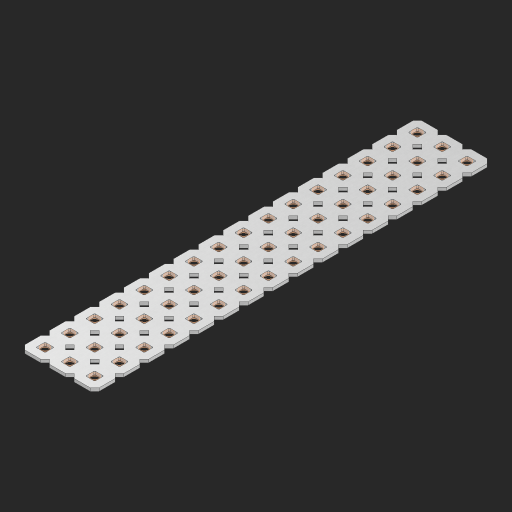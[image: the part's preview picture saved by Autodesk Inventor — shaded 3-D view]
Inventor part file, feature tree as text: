
AUTODESK INVENTOR PART (.ipt)
format: ipt  version: 2023 (Build 270158000, 158)  size: 834,560 bytes
history: native  units: in
note: dims shown in document units (in); Inventor stores cm internally (conversion verified against a paired STEP export)
features: other x49, extrude x47, sketch x2, pattern_linear x1
ambient origin geometry x8: Origin, YZ Plane, XZ Plane, XY Plane, X Axis, Y Axis, Z Axis, Center Point
bodies: Solid1 (feature_tree), Body (feature_tree)
feature tree (99):
  pattern_linear  "Rectangular Pattern1"  Spacing1=0.09in  [1 undecoded]
  sketch  "Sketch1"  dims[d1=0.5in]
  sketch  "Sketch2"  dims[d2=0.182in d3=0.09in d4=0.09in d5=0.09in d6=0.09in d7=0.09in d8=0.09in d9=0.09in d10=0.09in d11=0.02in d13=0.0in d14=0.172in d15=0.0625in d16=0.0in d19=0.5in d22=0.5in]
  other  "Srf1"
  other  "Srf126"
  other  "Srf127"
  other  "Srf128"
  other  "Srf129"
  other  "Srf130"
  other  "Srf131"
  other  "Srf250"
  other  "Srf251"
  other  "Srf252"
  other  "Srf253"
  other  "Srf254"
  other  "Srf255"
  other  "Srf256"
  other  "Srf257"
  other  "Srf258"
  other  "Srf268"
  other  "Srf269"
  other  "Srf270"
  other  "Srf271"
  other  "Srf272"
  other  "Srf273"
  other  "Srf274"
  other  "Srf275"
  other  "Srf276"
  other  "Srf277"
  other  "Srf278"
  other  "Srf279"
  other  "Srf280"
  other  "Srf281"
  other  "Srf282"
  other  "Srf283"
  other  "Srf293"
  other  "Srf294"
  other  "Srf295"
  other  "Srf296"
  other  "Srf297"
  other  "Srf298"
  other  "Srf299"
  other  "Srf300"
  other  "Srf301"
  other  "Srf302"
  other  "Srf303"
  other  "Srf304"
  other  "Srf305"
  other  "Srf306"
  other  "Srf307"
  other  "Srf308"
  other  "Circle"
  extrude  "ExtrusionSrf126"  Depth=0.09in
  extrude  "ExtrusionSrf127"  Depth=0.09in
  extrude  "ExtrusionSrf128"  Depth=0.09in
  extrude  "ExtrusionSrf129"  Depth=0.09in
  extrude  "ExtrusionSrf130"  Depth=0.09in
  extrude  "ExtrusionSrf131"  Depth=0.09in
  extrude  "ExtrusionSrf250"  Depth=0.09in
  extrude  "ExtrusionSrf251"  Depth=0.02in
  extrude  "ExtrusionSrf252"  TaperAngle=0.0deg  [1 undecoded]
  extrude  "ExtrusionSrf253"  Depth=0.5in
  extrude  "ExtrusionSrf254"  Depth=0.0625in TaperAngle=0.0deg
  extrude  "ExtrusionSrf255"  Depth=0.5in
  extrude  "ExtrusionSrf256"  Depth=0.5in
  extrude  "ExtrusionSrf257"  [1 undecoded]
  extrude  "ExtrusionSrf258"  [1 undecoded]
  extrude  "ExtrusionSrf268"  [1 undecoded]
  extrude  "ExtrusionSrf269"  [1 undecoded]
  extrude  "ExtrusionSrf270"  [1 undecoded]
  extrude  "ExtrusionSrf271"  [1 undecoded]
  extrude  "ExtrusionSrf272"  [1 undecoded]
  extrude  "ExtrusionSrf273"  [1 undecoded]
  extrude  "ExtrusionSrf274"  [1 undecoded]
  extrude  "ExtrusionSrf275"  [1 undecoded]
  extrude  "ExtrusionSrf276"  [1 undecoded]
  extrude  "ExtrusionSrf277"  [1 undecoded]
  extrude  "ExtrusionSrf278"  [1 undecoded]
  extrude  "ExtrusionSrf279"  [1 undecoded]
  extrude  "ExtrusionSrf280"  [1 undecoded]
  extrude  "ExtrusionSrf281"  [1 undecoded]
  extrude  "ExtrusionSrf282"  [1 undecoded]
  extrude  "ExtrusionSrf283"  [1 undecoded]
  extrude  "ExtrusionSrf293"  [1 undecoded]
  extrude  "ExtrusionSrf294"  [1 undecoded]
  extrude  "ExtrusionSrf295"  [1 undecoded]
  extrude  "ExtrusionSrf296"  [1 undecoded]
  extrude  "ExtrusionSrf297"  [1 undecoded]
  extrude  "ExtrusionSrf298"  [1 undecoded]
  extrude  "ExtrusionSrf299"  [1 undecoded]
  extrude  "ExtrusionSrf300"  [1 undecoded]
  extrude  "ExtrusionSrf301"  [1 undecoded]
  extrude  "ExtrusionSrf302"  [1 undecoded]
  extrude  "ExtrusionSrf303"  [1 undecoded]
  extrude  "ExtrusionSrf304"  [1 undecoded]
  extrude  "ExtrusionSrf305"  [1 undecoded]
  extrude  "ExtrusionSrf306"  [1 undecoded]
  extrude  "ExtrusionSrf307"  [1 undecoded]
  extrude  "ExtrusionSrf308"  [1 undecoded]
note: 36 required parameter values undecoded (feature->parameter linkage not recoverable at this tier; creation-order binding heuristic only, values carry confidence <= 0.55)
